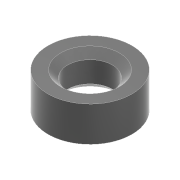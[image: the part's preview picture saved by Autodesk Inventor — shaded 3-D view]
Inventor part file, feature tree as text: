
AUTODESK INVENTOR PART (.ipt)
format: ipt  version: 2022 (Build 260153000, 153)  size: 101,888 bytes
history: native  units: mm
features: sketch x2, extrude x1, hole x1, chamfer x1
ambient origin geometry x8: Origin, YZ Plane, XZ Plane, XY Plane, X Axis, Y Axis, Z Axis, Center Point
bodies: Solid1 (feature_tree)
feature tree (5):
  extrude  "Extrusion1"  Depth=2.5mm TaperAngle=0.0deg
  hole  "Hole1"  [1 undecoded]
  chamfer  "Chamfer1"  [1 undecoded]
  sketch  "Sketch1"  dims[d0=6.0mm d1=2.5mm d2=0.0mm]
  sketch  "Sketch2"  dims[d3=3.2mm d4=6.0mm d5=4.0mm d6=2.0mm d7=90.0deg d8=8.0mm d9=20.594885mm d10=0.5mm d11=2.0mm d12=45.0deg]
note: 2 required parameter values undecoded (feature->parameter linkage not recoverable at this tier; creation-order binding heuristic only, values carry confidence <= 0.55)
